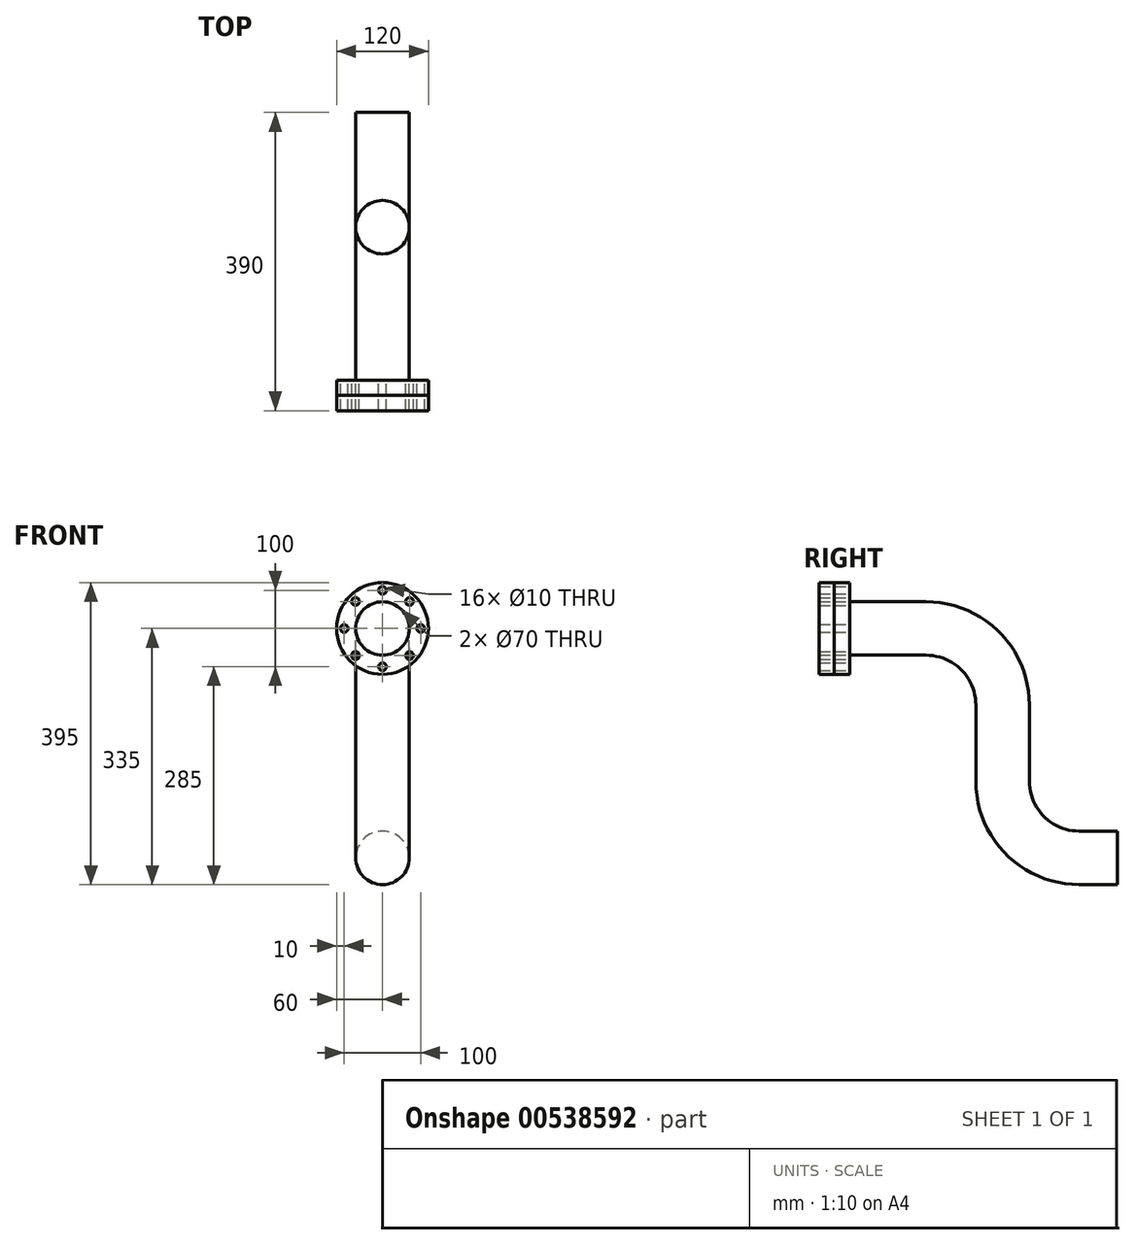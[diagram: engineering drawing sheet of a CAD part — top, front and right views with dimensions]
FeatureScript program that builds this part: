
annotation { "Feature Type Name" : "Feature", "Feature Type Description" : "" }
export const myFeature = defineFeature(function(context is Context, id is Id, definition is map)
    precondition{}
    {
        {
            var Q0;
            Q0=qCreatedBy(makeId("Front.planeOp"),FACE);
            var sketch = newSketch(context, id + "F0", { "sketchPlane" : qUnion([Q0])});
            skCircle(sketch, "E0", {"center": v(0, 0) * mm, "radius": 60 * mm});
            skLineSegment(sketch, "E1", {"start": v(0, 0) * mm, "end": v(0, 50) * mm});
            skCircle(sketch, "E2", {"center": v(0, 50) * mm, "radius": 5 * mm});
            skCircle(sketch, "E3.1.0", {"center": v(-35.36, 35.36) * mm, "radius": 5 * mm});
            skCircle(sketch, "E3.2.0", {"center": v(-50, 0) * mm, "radius": 5 * mm});
            skCircle(sketch, "E3.3.0", {"center": v(-35.36, -35.36) * mm, "radius": 5 * mm});
            skCircle(sketch, "E3.4.0", {"center": v(0, -50) * mm, "radius": 5 * mm});
            skCircle(sketch, "E3.5.0", {"center": v(35.36, -35.36) * mm, "radius": 5 * mm});
            skCircle(sketch, "E3.6.0", {"center": v(50, 0) * mm, "radius": 5 * mm});
            skCircle(sketch, "E3.7.0", {"center": v(35.36, 35.36) * mm, "radius": 5 * mm});
            skCircle(sketch, "E4", {"center": v(0, 0) * mm, "radius": 35 * mm});
            skSolve(sketch);
        }
        {
            var Q0;
            Q0 = qSketchRegion(id + "F0", true);
            extrude(context, id + "F1", {"entities" : qUnion([Q0]), "depth" : 20 * mm, "offsetDistance" : 25 * mm});
        }
        {
            var Q0;
            Q0=qCreatedBy(makeId("Front.planeOp"),FACE);
            var sketch = newSketch(context, id + "F2", { "sketchPlane" : qUnion([Q0])});
            skCircle(sketch, "E5", {"center": v(0, 0) * mm, "radius": 40 * mm});
            skCircle(sketch, "E6", {"center": v(0, 0) * mm, "radius": 35 * mm});
            skSolve(sketch);
        }
        {
            var Q0;
            Q0=qCreatedBy(makeId("Right.planeOp"),FACE);
            var sketch = newSketch(context, id + "F3", { "sketchPlane" : qUnion([Q0])});
            skLineSegment(sketch, "E7", {"start": v(0, 0) * mm, "end": v(100, 0) * mm});
            skLineSegment(sketch, "E8", {"start": v(200, -100) * mm, "end": v(200, -200) * mm});
            skLineSegment(sketch, "E9", {"start": v(300, -300) * mm, "end": v(350, -300) * mm});
            skPoint(sketch, "E10.visualSharp", {"position": v(200, 0) * mm});
            skArc(sketch, "E10.filletArc", {"start": v(200, -100) * mm, "mid": v(170.71, -29.29) * mm, "end": v(100, 0) * mm});
            skPoint(sketch, "E11.visualSharp", {"position": v(200, -300) * mm});
            skArc(sketch, "E11.filletArc", {"start": v(200, -200) * mm, "mid": v(229.29, -270.71) * mm, "end": v(300, -300) * mm});
            skSolve(sketch);
        }
        {
            var Q0;
            Q0=makeQuery(id+"F2.imprint","IMPRINT",FACE,{"disambiguationData":[TD([[makeQuery(id+"F2.imprint","IMPRINT",EDGE,{"derivedFrom":sQuery(id+"F2.wireOp",EDGE,"E6")}),1.0]])]});
            var Q1;
            Q1 = qConstructionFilter(qBodyType(qCreatedBy(id + "F3" ,EDGE), BodyType.WIRE), ConstructionObject.NO);
            sweep(context, id + "F4", {"operationType" : NewBodyOperationType.ADD, "profiles" : qUnion([Q0]), "path" : qUnion([Q1])});
        }
        {
            var Q0;
            Q0=makeQuery(id+"F1.opExtrude","CAP_FACE",FACE,{"disambiguationData":[OSD([sQuery(id+"F0.wireOp",EDGE,"E0"),sQuery(id+"F0.wireOp",EDGE,"E2"),sQuery(id+"F0.wireOp",EDGE,"E3.1.0"),sQuery(id+"F0.wireOp",EDGE,"E3.2.0"),sQuery(id+"F0.wireOp",EDGE,"E3.3.0"),sQuery(id+"F0.wireOp",EDGE,"E3.4.0"),sQuery(id+"F0.wireOp",EDGE,"E3.5.0"),sQuery(id+"F0.wireOp",EDGE,"E3.6.0"),sQuery(id+"F0.wireOp",EDGE,"E3.7.0"),sQuery(id+"F0.wireOp",EDGE,"E4")])],"isStart":false});
            extrude(context, id + "F5", {"entities" : qUnion([Q0]), "depth" : 20 * mm, "offsetDistance" : 25 * mm});
        }
    });
